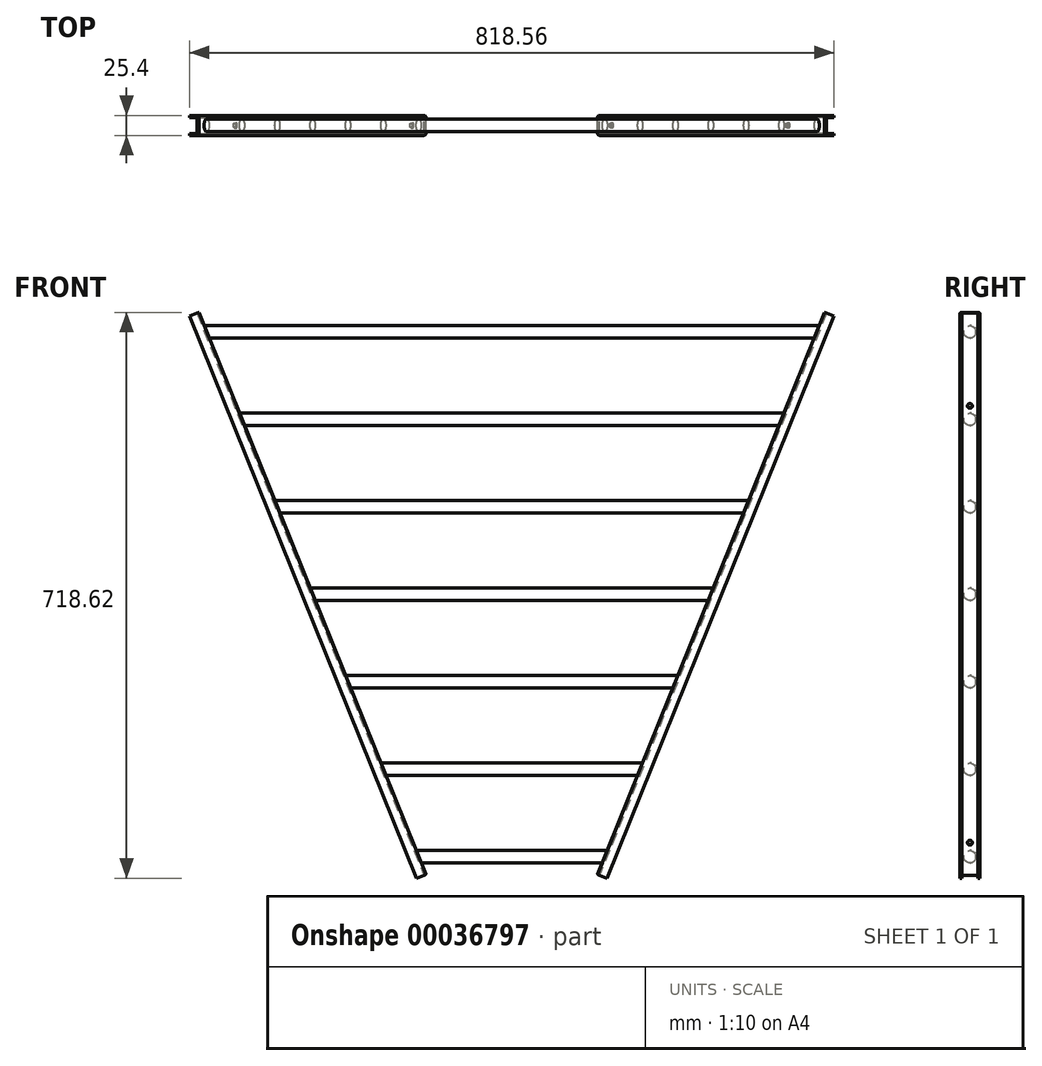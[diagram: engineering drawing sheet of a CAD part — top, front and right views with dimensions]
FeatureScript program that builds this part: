
annotation { "Feature Type Name" : "Feature", "Feature Type Description" : "" }
export const myFeature = defineFeature(function(context is Context, id is Id, definition is map)
    precondition{}
    {
        {
            var Q0;
            Q0=qCreatedBy(makeId("Front.planeOp"),FACE);
            var sketch = newSketch(context, id + "F0", { "sketchPlane" : qUnion([Q0])});
            skLineSegment(sketch, "E0", {"start": v(0, 0) * mm, "end": v(-432.03, 1069.3) * mm});
            skLineSegment(sketch, "E1", {"start": v(-432.03, 1069.3) * mm, "end": v(432.03, 1069.3) * mm});
            skLineSegment(sketch, "E2", {"start": v(432.03, 1069.3) * mm, "end": v(0, 0) * mm});
            skLineSegment(sketch, "E3.direction1", {"start": v(-432.03, 1069.3) * mm, "end": v(-432.03, 1069.3) * mm});
            skLineSegment(sketch, "E4.0.1.0", {"start": v(-432.03, 966.12) * mm, "end": v(432.03, 966.12) * mm});
            skLineSegment(sketch, "E4.1.0.0", {"start": v(-406.63, 1069.3) * mm, "end": v(457.43, 1069.3) * mm});
            skLineSegment(sketch, "E4.1.1.0", {"start": v(-406.63, 966.12) * mm, "end": v(457.43, 966.12) * mm});
            skLineSegment(sketch, "E4.direction1", {"start": v(-432.03, 1069.3) * mm, "end": v(-406.63, 1069.3) * mm, "construction": true});
            skLineSegment(sketch, "E4.direction2", {"start": v(-432.03, 1069.3) * mm, "end": v(-432.03, 966.12) * mm, "construction": true});
            skLineSegment(sketch, "E5.0.1.0", {"start": v(-406.63, 855) * mm, "end": v(457.43, 855) * mm});
            skLineSegment(sketch, "E5.0.2.0", {"start": v(-406.63, 743.87) * mm, "end": v(457.43, 743.87) * mm});
            skLineSegment(sketch, "E5.0.3.0", {"start": v(-406.63, 632.75) * mm, "end": v(457.43, 632.75) * mm});
            skLineSegment(sketch, "E5.0.4.0", {"start": v(-406.63, 521.62) * mm, "end": v(457.43, 521.62) * mm});
            skLineSegment(sketch, "E5.0.5.0", {"start": v(-406.63, 410.5) * mm, "end": v(457.43, 410.5) * mm});
            skLineSegment(sketch, "E5.0.6.0", {"start": v(-406.63, 299.37) * mm, "end": v(457.43, 299.37) * mm});
            skLineSegment(sketch, "E5.1.0.0", {"start": v(-381.23, 966.12) * mm, "end": v(482.83, 966.12) * mm});
            skLineSegment(sketch, "E5.1.1.0", {"start": v(-381.23, 855) * mm, "end": v(482.83, 855) * mm});
            skLineSegment(sketch, "E5.1.2.0", {"start": v(-381.23, 743.87) * mm, "end": v(482.83, 743.87) * mm});
            skLineSegment(sketch, "E5.1.3.0", {"start": v(-381.23, 632.75) * mm, "end": v(482.83, 632.75) * mm});
            skLineSegment(sketch, "E5.1.4.0", {"start": v(-381.23, 521.62) * mm, "end": v(482.83, 521.62) * mm});
            skLineSegment(sketch, "E5.1.5.0", {"start": v(-381.23, 410.5) * mm, "end": v(482.83, 410.5) * mm});
            skLineSegment(sketch, "E5.1.6.0", {"start": v(-381.23, 299.37) * mm, "end": v(482.83, 299.37) * mm});
            skLineSegment(sketch, "E5.2.0.0", {"start": v(-355.83, 966.12) * mm, "end": v(508.23, 966.12) * mm});
            skLineSegment(sketch, "E5.2.1.0", {"start": v(-355.83, 855) * mm, "end": v(508.23, 855) * mm});
            skLineSegment(sketch, "E5.2.2.0", {"start": v(-355.83, 743.87) * mm, "end": v(508.23, 743.87) * mm});
            skLineSegment(sketch, "E5.2.3.0", {"start": v(-355.83, 632.75) * mm, "end": v(508.23, 632.75) * mm});
            skLineSegment(sketch, "E5.2.4.0", {"start": v(-355.83, 521.62) * mm, "end": v(508.23, 521.62) * mm});
            skLineSegment(sketch, "E5.2.5.0", {"start": v(-355.83, 410.5) * mm, "end": v(508.23, 410.5) * mm});
            skLineSegment(sketch, "E5.2.6.0", {"start": v(-355.83, 299.37) * mm, "end": v(508.23, 299.37) * mm});
            skLineSegment(sketch, "E5.direction1", {"start": v(-406.63, 966.12) * mm, "end": v(-381.23, 966.12) * mm, "construction": true});
            skLineSegment(sketch, "E5.direction2", {"start": v(-406.63, 966.12) * mm, "end": v(-406.63, 855) * mm, "construction": true});
            skPoint(sketch, "E6", {"position": v(-120.95, 299.37) * mm});
            skPoint(sketch, "E7", {"position": v(120.95, 299.37) * mm});
            skPoint(sketch, "E8", {"position": v(-390.34, 966.12) * mm});
            skPoint(sketch, "E8.positionSnap0", {"position": v(-393.93, 966.12) * mm});
            skSolve(sketch);
        }
        {
            var Q0;
            Q0=sQuery(id+"F0.wireOp",VERTEX,"E6");
            var Q1;
            Q1=sQuery(id+"F0.wireOp",EDGE,"E0");
            cPlane(context, id + "F1", {"entities" : qUnion([Q0, Q1]), "cplaneType" : CPlaneType.LINE_POINT, "offset" : 152.4 * mm, "width" : 152.4 * mm, "height" : 152.4 * mm});
        }
        {
            var Q0;
            Q0=qCreatedBy(id+"F1.planeOp",FACE);
            var sketch = newSketch(context, id + "F2", { "sketchPlane" : qUnion([Q0])});
            skLineSegment(sketch, "E9", {"start": v(0, 0) * mm, "end": v(0, -10.16) * mm});
            skLineSegment(sketch, "E10", {"start": v(0, -10.16) * mm, "end": v(-10.16, -10.16) * mm});
            skLineSegment(sketch, "E11", {"start": v(-10.16, -10.16) * mm, "end": v(-10.16, -12.7) * mm});
            skLineSegment(sketch, "E12", {"start": v(-10.16, -12.7) * mm, "end": v(0, -12.7) * mm});
            skLineSegment(sketch, "E13", {"start": v(2.54, -10.16) * mm, "end": v(2.54, 0) * mm});
            skLineSegment(sketch, "E14.MirrorCS", {"start": v(0, 10.16) * mm, "end": v(-10.16, 10.16) * mm});
            skLineSegment(sketch, "E15.MirrorCS", {"start": v(-10.16, 10.16) * mm, "end": v(-10.16, 12.7) * mm});
            skLineSegment(sketch, "E16.MirrorCS", {"start": v(-10.16, 12.7) * mm, "end": v(0, 12.7) * mm});
            skLineSegment(sketch, "E17.MirrorCS", {"start": v(2.54, 10.16) * mm, "end": v(2.54, 0) * mm});
            skLineSegment(sketch, "E18.MirrorCS", {"start": v(0, 0) * mm, "end": v(0, 10.16) * mm});
            skPoint(sketch, "E19.visualSharp", {"position": v(2.54, -12.7) * mm});
            skArc(sketch, "E19.filletArc", {"start": v(0, -12.7) * mm, "mid": v(1.8, -11.96) * mm, "end": v(2.54, -10.16) * mm});
            skPoint(sketch, "E20.visualSharp", {"position": v(2.54, 12.7) * mm});
            skArc(sketch, "E20.filletArc", {"start": v(2.54, 10.16) * mm, "mid": v(1.8, 11.96) * mm, "end": v(0, 12.7) * mm});
            skSolve(sketch);
        }
        {
            var Q0;
            Q0 = qSketchRegion(id + "F2", true);
            extrude(context, id + "F3", {"entities" : qUnion([Q0]), "depth" : 744.52 * mm, "hasSecondDirection" : true, "secondDirectionOppositeDirection" : true, "secondDirectionDepth" : 25.4 * mm});
        }
        {
            var Q0;
            Q0=makeQuery(id+"F3.opExtrude","SWEPT_FACE",FACE,{"disambiguationData":[OSD([sQuery(id+"F2.wireOp",EDGE,"E13"),sQuery(id+"F2.wireOp",EDGE,"E17.MirrorCS")])]});
            var sketch = newSketch(context, id + "F4", { "sketchPlane" : qUnion([Q0])});
            skCircle(sketch, "E21", {"center": v(0, 940.4) * mm, "radius": 3.18 * mm});
            skCircle(sketch, "E22", {"center": v(0, 341.93) * mm, "radius": 3.18 * mm});
            skSolve(sketch);
        }
        {
            var Q0;
            Q0 = qSketchRegion(id + "F4", true);
            extrude(context, id + "F5", {"entities" : qUnion([Q0]), "operationType" : NewBodyOperationType.REMOVE, "endBound" : BoundingType.UP_TO_NEXT, "oppositeDirection" : true, "depth" : 25.4 * mm});
        }
        {
            var Q0;
            Q0=makeQuery(id+"F3.opExtrude","SWEPT_BODY",BODY,{"disambiguationData":[OSD([sQuery(id+"F2.wireOp",EDGE,"E9"),sQuery(id+"F2.wireOp",EDGE,"E10"),sQuery(id+"F2.wireOp",EDGE,"E11"),sQuery(id+"F2.wireOp",EDGE,"E12"),sQuery(id+"F2.wireOp",EDGE,"E13"),sQuery(id+"F2.wireOp",EDGE,"E14.MirrorCS"),sQuery(id+"F2.wireOp",EDGE,"E15.MirrorCS"),sQuery(id+"F2.wireOp",EDGE,"E16.MirrorCS"),sQuery(id+"F2.wireOp",EDGE,"E17.MirrorCS"),sQuery(id+"F2.wireOp",EDGE,"E18.MirrorCS"),sQuery(id+"F2.wireOp",EDGE,"E19.filletArc"),sQuery(id+"F2.wireOp",EDGE,"E20.filletArc")])]});
            var Q1;
            Q1=qCreatedBy(makeId("Right.planeOp"),FACE);
            mirror(context, id + "F6", {"entities" : qUnion([Q0]), "mirrorPlane" : qUnion([Q1])});
        }
        {
            var Q0;
            Q0=qCreatedBy(makeId("Right.planeOp"),FACE);
            var sketch = newSketch(context, id + "F7", { "sketchPlane" : qUnion([Q0])});
            skPoint(sketch, "E23.0", {"position": v(0, 966.12) * mm});
            skPoint(sketch, "E24.0", {"position": v(0, 855) * mm});
            skPoint(sketch, "E25.0", {"position": v(0, 743.87) * mm});
            skPoint(sketch, "E26.0", {"position": v(0, 632.75) * mm});
            skPoint(sketch, "E27.0", {"position": v(0, 521.62) * mm});
            skPoint(sketch, "E28.0", {"position": v(0, 410.5) * mm});
            skPoint(sketch, "E29.0", {"position": v(0, 299.37) * mm});
            skCircle(sketch, "E30", {"center": v(0, 966.12) * mm, "radius": 7.94 * mm});
            skCircle(sketch, "E31", {"center": v(0, 855) * mm, "radius": 7.94 * mm});
            skCircle(sketch, "E32", {"center": v(0, 743.87) * mm, "radius": 7.94 * mm});
            skCircle(sketch, "E33", {"center": v(0, 632.75) * mm, "radius": 7.94 * mm});
            skCircle(sketch, "E34", {"center": v(0, 521.62) * mm, "radius": 7.94 * mm});
            skCircle(sketch, "E35", {"center": v(0, 410.5) * mm, "radius": 7.94 * mm});
            skCircle(sketch, "E36", {"center": v(0, 299.37) * mm, "radius": 7.94 * mm});
            skSolve(sketch);
        }
        {
            var Q0;
            Q0 = qSketchRegion(id + "F7", true);
            extrude(context, id + "F8", {"entities" : qUnion([Q0]), "operationType" : NewBodyOperationType.ADD, "endBound" : BoundingType.UP_TO_NEXT, "depth" : 25.4 * mm, "hasSecondDirection" : true, "secondDirectionBound" : SecondDirectionBoundingType.UP_TO_NEXT, "secondDirectionOppositeDirection" : true, "secondDirectionDepth" : 25.4 * mm});
        }
    });
